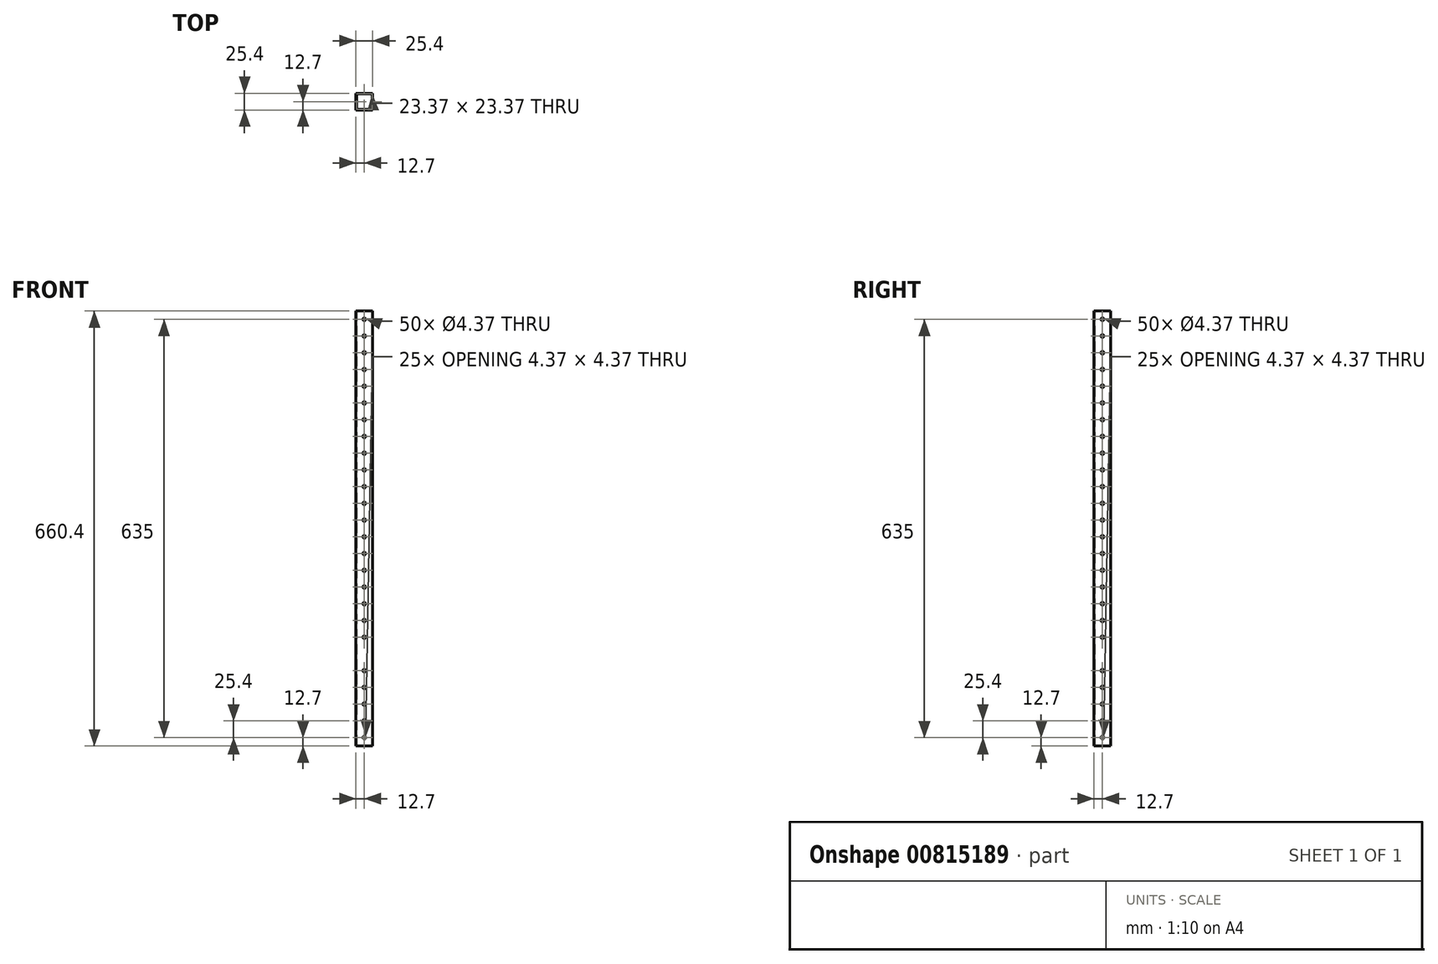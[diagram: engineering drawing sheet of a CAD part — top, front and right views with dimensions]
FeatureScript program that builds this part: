
annotation { "Feature Type Name" : "Feature", "Feature Type Description" : "" }
export const myFeature = defineFeature(function(context is Context, id is Id, definition is map)
    precondition{}
    {
        {
            var Q0;
            Q0=qCreatedBy(makeId("Top.planeOp"),FACE);
            var sketch = newSketch(context, id + "F0", { "sketchPlane" : qUnion([Q0])});
            skLineSegment(sketch, "E0.bottom", {"start": v(0, 0) * mm, "end": v(25.4, 0) * mm});
            skLineSegment(sketch, "E0.top", {"start": v(0, -25.4) * mm, "end": v(25.4, -25.4) * mm});
            skLineSegment(sketch, "E0.left", {"start": v(0, 0) * mm, "end": v(0, -25.4) * mm});
            skLineSegment(sketch, "E0.right", {"start": v(25.4, 0) * mm, "end": v(25.4, -25.4) * mm});
            skLineSegment(sketch, "E1.bottom", {"start": v(1.02, -1.02) * mm, "end": v(24.38, -1.02) * mm});
            skLineSegment(sketch, "E1.top", {"start": v(1.02, -24.38) * mm, "end": v(24.38, -24.38) * mm});
            skLineSegment(sketch, "E1.left", {"start": v(1.02, -1.02) * mm, "end": v(1.02, -24.38) * mm});
            skLineSegment(sketch, "E1.right", {"start": v(24.38, -1.02) * mm, "end": v(24.38, -24.38) * mm});
            skSolve(sketch);
        }
        {
            var Q0;
            Q0=makeQuery(id+"F0.imprint","IMPRINT",FACE,{"disambiguationData":[TD([[makeQuery(id+"F0.imprint","IMPRINT",EDGE,{"derivedFrom":sQuery(id+"F0.wireOp",EDGE,"E0.bottom")}),-1.0]])]});
            extrude(context, id + "F1", {"entities" : qUnion([Q0]), "depth" : 508 * mm, "offsetDistance" : 25.4 * mm});
        }
        {
            var Q0;
            Q0=makeQuery(id+"F1.opExtrude","SWEPT_FACE",FACE,{"disambiguationData":[OSD([sQuery(id+"F0.wireOp",EDGE,"E0.top")])]});
            var sketch = newSketch(context, id + "F2", { "sketchPlane" : qUnion([Q0])});
            skCircle(sketch, "E2", {"center": v(12.7, 12.7) * mm, "radius": 2.18 * mm});
            skCircle(sketch, "E3.0.1.0", {"center": v(12.7, 38.1) * mm, "radius": 2.18 * mm});
            skCircle(sketch, "E3.0.2.0", {"center": v(12.7, 63.5) * mm, "radius": 2.18 * mm});
            skCircle(sketch, "E3.0.3.0", {"center": v(12.7, 88.9) * mm, "radius": 2.18 * mm});
            skCircle(sketch, "E3.0.4.0", {"center": v(12.7, 114.3) * mm, "radius": 2.18 * mm});
            skCircle(sketch, "E3.0.5.0", {"center": v(12.7, 139.7) * mm, "radius": 2.18 * mm});
            skCircle(sketch, "E3.0.6.0", {"center": v(12.7, 165.1) * mm, "radius": 2.18 * mm});
            skCircle(sketch, "E3.0.7.0", {"center": v(12.7, 190.5) * mm, "radius": 2.18 * mm});
            skCircle(sketch, "E3.0.8.0", {"center": v(12.7, 215.9) * mm, "radius": 2.18 * mm});
            skCircle(sketch, "E3.0.9.0", {"center": v(12.7, 241.3) * mm, "radius": 2.18 * mm});
            skCircle(sketch, "E3.0.10.0", {"center": v(12.7, 266.7) * mm, "radius": 2.18 * mm});
            skCircle(sketch, "E3.0.11.0", {"center": v(12.7, 292.1) * mm, "radius": 2.18 * mm});
            skCircle(sketch, "E3.0.12.0", {"center": v(12.7, 317.5) * mm, "radius": 2.18 * mm});
            skCircle(sketch, "E3.0.13.0", {"center": v(12.7, 342.9) * mm, "radius": 2.18 * mm});
            skCircle(sketch, "E3.0.14.0", {"center": v(12.7, 368.3) * mm, "radius": 2.18 * mm});
            skCircle(sketch, "E3.0.15.0", {"center": v(12.7, 393.7) * mm, "radius": 2.18 * mm});
            skCircle(sketch, "E3.0.16.0", {"center": v(12.7, 419.1) * mm, "radius": 2.18 * mm});
            skCircle(sketch, "E3.0.17.0", {"center": v(12.7, 444.5) * mm, "radius": 2.18 * mm});
            skCircle(sketch, "E3.0.18.0", {"center": v(12.7, 469.9) * mm, "radius": 2.18 * mm});
            skCircle(sketch, "E3.0.19.0", {"center": v(12.7, 495.3) * mm, "radius": 2.18 * mm});
            skCircle(sketch, "E3.0.20.0", {"center": v(12.7, 520.7) * mm, "radius": 2.18 * mm});
            skCircle(sketch, "E3.0.21.0", {"center": v(12.7, 546.1) * mm, "radius": 2.18 * mm});
            skCircle(sketch, "E3.0.22.0", {"center": v(12.7, 571.5) * mm, "radius": 2.18 * mm});
            skCircle(sketch, "E3.0.23.0", {"center": v(12.7, 596.9) * mm, "radius": 2.18 * mm});
            skCircle(sketch, "E3.0.24.0", {"center": v(12.7, 622.3) * mm, "radius": 2.18 * mm});
            skLineSegment(sketch, "E3.direction1", {"start": v(12.7, 12.7) * mm, "end": v(38.1, 12.7) * mm, "construction": true});
            skLineSegment(sketch, "E3.direction2", {"start": v(12.7, 12.7) * mm, "end": v(12.7, 38.1) * mm, "construction": true});
            skSolve(sketch);
        }
        {
            var Q0;
            Q0=makeQuery(id+"F2.imprint","IMPRINT",FACE,{"disambiguationData":[TD([[makeQuery(id+"F2.imprint","IMPRINT",EDGE,{"derivedFrom":sQuery(id+"F2.wireOp",EDGE,"E2")}),1.0]])]});
            var Q1;
            Q1=makeQuery(id+"F2.imprint","IMPRINT",FACE,{"disambiguationData":[TD([[makeQuery(id+"F2.imprint","IMPRINT",EDGE,{"derivedFrom":sQuery(id+"F2.wireOp",EDGE,"E3.0.1.0")}),1.0]])]});
            var Q2;
            Q2=makeQuery(id+"F2.imprint","IMPRINT",FACE,{"disambiguationData":[TD([[makeQuery(id+"F2.imprint","IMPRINT",EDGE,{"derivedFrom":sQuery(id+"F2.wireOp",EDGE,"E3.0.9.0")}),1.0]])]});
            var Q3;
            Q3=makeQuery(id+"F2.imprint","IMPRINT",FACE,{"disambiguationData":[TD([[makeQuery(id+"F2.imprint","IMPRINT",EDGE,{"derivedFrom":sQuery(id+"F2.wireOp",EDGE,"E3.0.8.0")}),1.0]])]});
            var Q4;
            Q4=makeQuery(id+"F2.imprint","IMPRINT",FACE,{"disambiguationData":[TD([[makeQuery(id+"F2.imprint","IMPRINT",EDGE,{"derivedFrom":sQuery(id+"F2.wireOp",EDGE,"E3.0.7.0")}),1.0]])]});
            var Q5;
            Q5=makeQuery(id+"F2.imprint","IMPRINT",FACE,{"disambiguationData":[TD([[makeQuery(id+"F2.imprint","IMPRINT",EDGE,{"derivedFrom":sQuery(id+"F2.wireOp",EDGE,"E3.0.6.0")}),1.0]])]});
            var Q6;
            Q6=makeQuery(id+"F2.imprint","IMPRINT",FACE,{"disambiguationData":[TD([[makeQuery(id+"F2.imprint","IMPRINT",EDGE,{"derivedFrom":sQuery(id+"F2.wireOp",EDGE,"E3.0.5.0")}),1.0]])]});
            var Q7;
            Q7=makeQuery(id+"F2.imprint","IMPRINT",FACE,{"disambiguationData":[TD([[makeQuery(id+"F2.imprint","IMPRINT",EDGE,{"derivedFrom":sQuery(id+"F2.wireOp",EDGE,"E3.0.4.0")}),1.0]])]});
            var Q8;
            Q8=makeQuery(id+"F2.imprint","IMPRINT",FACE,{"disambiguationData":[TD([[makeQuery(id+"F2.imprint","IMPRINT",EDGE,{"derivedFrom":sQuery(id+"F2.wireOp",EDGE,"E3.0.3.0")}),1.0]])]});
            var Q9;
            Q9=makeQuery(id+"F2.imprint","IMPRINT",FACE,{"disambiguationData":[TD([[makeQuery(id+"F2.imprint","IMPRINT",EDGE,{"derivedFrom":sQuery(id+"F2.wireOp",EDGE,"E3.0.2.0")}),1.0]])]});
            var Q10;
            Q10=makeQuery(id+"F2.imprint","IMPRINT",FACE,{"disambiguationData":[TD([[makeQuery(id+"F2.imprint","IMPRINT",EDGE,{"derivedFrom":sQuery(id+"F2.wireOp",EDGE,"E3.0.10.0")}),1.0]])]});
            var Q11;
            Q11=makeQuery(id+"F2.imprint","IMPRINT",FACE,{"disambiguationData":[TD([[makeQuery(id+"F2.imprint","IMPRINT",EDGE,{"derivedFrom":sQuery(id+"F2.wireOp",EDGE,"E3.0.11.0")}),1.0]])]});
            var Q12;
            Q12=makeQuery(id+"F2.imprint","IMPRINT",FACE,{"disambiguationData":[TD([[makeQuery(id+"F2.imprint","IMPRINT",EDGE,{"derivedFrom":sQuery(id+"F2.wireOp",EDGE,"E3.0.12.0")}),1.0]])]});
            var Q13;
            Q13=makeQuery(id+"F2.imprint","IMPRINT",FACE,{"disambiguationData":[TD([[makeQuery(id+"F2.imprint","IMPRINT",EDGE,{"derivedFrom":sQuery(id+"F2.wireOp",EDGE,"E3.0.13.0")}),1.0]])]});
            var Q14;
            Q14=makeQuery(id+"F2.imprint","IMPRINT",FACE,{"disambiguationData":[TD([[makeQuery(id+"F2.imprint","IMPRINT",EDGE,{"derivedFrom":sQuery(id+"F2.wireOp",EDGE,"E3.0.14.0")}),1.0]])]});
            var Q15;
            Q15=makeQuery(id+"F2.imprint","IMPRINT",FACE,{"disambiguationData":[TD([[makeQuery(id+"F2.imprint","IMPRINT",EDGE,{"derivedFrom":sQuery(id+"F2.wireOp",EDGE,"E3.0.15.0")}),1.0]])]});
            var Q16;
            Q16=makeQuery(id+"F2.imprint","IMPRINT",FACE,{"disambiguationData":[TD([[makeQuery(id+"F2.imprint","IMPRINT",EDGE,{"derivedFrom":sQuery(id+"F2.wireOp",EDGE,"E3.0.16.0")}),1.0]])]});
            var Q17;
            Q17=makeQuery(id+"F2.imprint","IMPRINT",FACE,{"disambiguationData":[TD([[makeQuery(id+"F2.imprint","IMPRINT",EDGE,{"derivedFrom":sQuery(id+"F2.wireOp",EDGE,"E3.0.17.0")}),1.0]])]});
            var Q18;
            Q18=makeQuery(id+"F2.imprint","IMPRINT",FACE,{"disambiguationData":[TD([[makeQuery(id+"F2.imprint","IMPRINT",EDGE,{"derivedFrom":sQuery(id+"F2.wireOp",EDGE,"E3.0.18.0")}),1.0]])]});
            var Q19;
            Q19=makeQuery(id+"F2.imprint","IMPRINT",FACE,{"disambiguationData":[TD([[makeQuery(id+"F2.imprint","IMPRINT",EDGE,{"derivedFrom":sQuery(id+"F2.wireOp",EDGE,"E3.0.19.0")}),1.0]])]});
            var Q20;
            Q20=makeQuery(id+"F2.imprint","IMPRINT",FACE,{"disambiguationData":[TD([[makeQuery(id+"F2.imprint","IMPRINT",EDGE,{"derivedFrom":sQuery(id+"F2.wireOp",EDGE,"E3.0.20.0")}),1.0]])]});
            var Q21;
            Q21=makeQuery(id+"F2.imprint","IMPRINT",FACE,{"disambiguationData":[TD([[makeQuery(id+"F2.imprint","IMPRINT",EDGE,{"derivedFrom":sQuery(id+"F2.wireOp",EDGE,"E3.0.21.0")}),1.0]])]});
            var Q22;
            Q22=makeQuery(id+"F2.imprint","IMPRINT",FACE,{"disambiguationData":[TD([[makeQuery(id+"F2.imprint","IMPRINT",EDGE,{"derivedFrom":sQuery(id+"F2.wireOp",EDGE,"E3.0.22.0")}),1.0]])]});
            var Q23;
            Q23=makeQuery(id+"F2.imprint","IMPRINT",FACE,{"disambiguationData":[TD([[makeQuery(id+"F2.imprint","IMPRINT",EDGE,{"derivedFrom":sQuery(id+"F2.wireOp",EDGE,"E3.0.23.0")}),1.0]])]});
            var Q24;
            Q24=makeQuery(id+"F2.imprint","IMPRINT",FACE,{"disambiguationData":[TD([[makeQuery(id+"F2.imprint","IMPRINT",EDGE,{"derivedFrom":sQuery(id+"F2.wireOp",EDGE,"E3.0.24.0")}),1.0]])]});
            extrude(context, id + "F3", {"entities" : qUnion([Q0, Q1, Q2, Q3, Q4, Q5, Q6, Q7, Q8, Q9, Q10, Q11, Q12, Q13, Q14, Q15, Q16, Q17, Q18, Q19, Q20, Q21, Q22, Q23, Q24]), "operationType" : NewBodyOperationType.REMOVE, "oppositeDirection" : true, "depth" : 25.4 * mm, "offsetDistance" : 25.4 * mm});
        }
        {
            var Q0;
            Q0=makeQuery(id+"F1.opExtrude","SWEPT_FACE",FACE,{"disambiguationData":[OSD([sQuery(id+"F0.wireOp",EDGE,"E0.left")])]});
            var sketch = newSketch(context, id + "F4", { "sketchPlane" : qUnion([Q0])});
            skCircle(sketch, "E4", {"center": v(12.7, 12.7) * mm, "radius": 2.18 * mm});
            skCircle(sketch, "E5.0.1.0", {"center": v(12.7, 38.1) * mm, "radius": 2.18 * mm});
            skCircle(sketch, "E5.0.2.0", {"center": v(12.7, 63.5) * mm, "radius": 2.18 * mm});
            skCircle(sketch, "E5.0.3.0", {"center": v(12.7, 88.9) * mm, "radius": 2.18 * mm});
            skCircle(sketch, "E5.0.4.0", {"center": v(12.7, 114.3) * mm, "radius": 2.18 * mm});
            skCircle(sketch, "E5.0.5.0", {"center": v(12.7, 139.7) * mm, "radius": 2.18 * mm});
            skCircle(sketch, "E5.0.6.0", {"center": v(12.7, 165.1) * mm, "radius": 2.18 * mm});
            skCircle(sketch, "E5.0.7.0", {"center": v(12.7, 190.5) * mm, "radius": 2.18 * mm});
            skCircle(sketch, "E5.0.8.0", {"center": v(12.7, 215.9) * mm, "radius": 2.18 * mm});
            skCircle(sketch, "E5.0.9.0", {"center": v(12.7, 241.3) * mm, "radius": 2.18 * mm});
            skCircle(sketch, "E5.0.10.0", {"center": v(12.7, 266.7) * mm, "radius": 2.18 * mm});
            skCircle(sketch, "E5.0.11.0", {"center": v(12.7, 292.1) * mm, "radius": 2.18 * mm});
            skCircle(sketch, "E5.0.12.0", {"center": v(12.7, 317.5) * mm, "radius": 2.18 * mm});
            skCircle(sketch, "E5.0.13.0", {"center": v(12.7, 342.9) * mm, "radius": 2.18 * mm});
            skCircle(sketch, "E5.0.14.0", {"center": v(12.7, 368.3) * mm, "radius": 2.18 * mm});
            skCircle(sketch, "E5.0.15.0", {"center": v(12.7, 393.7) * mm, "radius": 2.18 * mm});
            skCircle(sketch, "E5.0.16.0", {"center": v(12.7, 419.1) * mm, "radius": 2.18 * mm});
            skCircle(sketch, "E5.0.17.0", {"center": v(12.7, 444.5) * mm, "radius": 2.18 * mm});
            skCircle(sketch, "E5.0.18.0", {"center": v(12.7, 469.9) * mm, "radius": 2.18 * mm});
            skCircle(sketch, "E5.0.19.0", {"center": v(12.7, 495.3) * mm, "radius": 2.18 * mm});
            skCircle(sketch, "E5.0.20.0", {"center": v(12.7, 520.7) * mm, "radius": 2.18 * mm});
            skCircle(sketch, "E5.0.21.0", {"center": v(12.7, 546.1) * mm, "radius": 2.18 * mm});
            skCircle(sketch, "E5.0.22.0", {"center": v(12.7, 571.5) * mm, "radius": 2.18 * mm});
            skCircle(sketch, "E5.0.23.0", {"center": v(12.7, 596.9) * mm, "radius": 2.18 * mm});
            skCircle(sketch, "E5.0.24.0", {"center": v(12.7, 622.3) * mm, "radius": 2.18 * mm});
            skLineSegment(sketch, "E5.direction1", {"start": v(12.7, 12.7) * mm, "end": v(38.1, 12.7) * mm, "construction": true});
            skLineSegment(sketch, "E5.direction2", {"start": v(12.7, 12.7) * mm, "end": v(12.7, 38.1) * mm, "construction": true});
            skSolve(sketch);
        }
        {
            var Q0;
            Q0=makeQuery(id+"F4.imprint","IMPRINT",FACE,{"disambiguationData":[TD([[makeQuery(id+"F4.imprint","IMPRINT",EDGE,{"derivedFrom":sQuery(id+"F4.wireOp",EDGE,"E4")}),1.0]])]});
            var Q1;
            Q1=makeQuery(id+"F4.imprint","IMPRINT",FACE,{"disambiguationData":[TD([[makeQuery(id+"F4.imprint","IMPRINT",EDGE,{"derivedFrom":sQuery(id+"F4.wireOp",EDGE,"E5.0.1.0")}),1.0]])]});
            var Q2;
            Q2=makeQuery(id+"F4.imprint","IMPRINT",FACE,{"disambiguationData":[TD([[makeQuery(id+"F4.imprint","IMPRINT",EDGE,{"derivedFrom":sQuery(id+"F4.wireOp",EDGE,"E5.0.2.0")}),1.0]])]});
            var Q3;
            Q3=makeQuery(id+"F4.imprint","IMPRINT",FACE,{"disambiguationData":[TD([[makeQuery(id+"F4.imprint","IMPRINT",EDGE,{"derivedFrom":sQuery(id+"F4.wireOp",EDGE,"E5.0.3.0")}),1.0]])]});
            var Q4;
            Q4=makeQuery(id+"F4.imprint","IMPRINT",FACE,{"disambiguationData":[TD([[makeQuery(id+"F4.imprint","IMPRINT",EDGE,{"derivedFrom":sQuery(id+"F4.wireOp",EDGE,"E5.0.4.0")}),1.0]])]});
            var Q5;
            Q5=makeQuery(id+"F4.imprint","IMPRINT",FACE,{"disambiguationData":[TD([[makeQuery(id+"F4.imprint","IMPRINT",EDGE,{"derivedFrom":sQuery(id+"F4.wireOp",EDGE,"E5.0.5.0")}),1.0]])]});
            var Q6;
            Q6=makeQuery(id+"F4.imprint","IMPRINT",FACE,{"disambiguationData":[TD([[makeQuery(id+"F4.imprint","IMPRINT",EDGE,{"derivedFrom":sQuery(id+"F4.wireOp",EDGE,"E5.0.6.0")}),1.0]])]});
            var Q7;
            Q7=makeQuery(id+"F4.imprint","IMPRINT",FACE,{"disambiguationData":[TD([[makeQuery(id+"F4.imprint","IMPRINT",EDGE,{"derivedFrom":sQuery(id+"F4.wireOp",EDGE,"E5.0.7.0")}),1.0]])]});
            var Q8;
            Q8=makeQuery(id+"F4.imprint","IMPRINT",FACE,{"disambiguationData":[TD([[makeQuery(id+"F4.imprint","IMPRINT",EDGE,{"derivedFrom":sQuery(id+"F4.wireOp",EDGE,"E5.0.8.0")}),1.0]])]});
            var Q9;
            Q9=makeQuery(id+"F4.imprint","IMPRINT",FACE,{"disambiguationData":[TD([[makeQuery(id+"F4.imprint","IMPRINT",EDGE,{"derivedFrom":sQuery(id+"F4.wireOp",EDGE,"E5.0.9.0")}),1.0]])]});
            var Q10;
            Q10=makeQuery(id+"F4.imprint","IMPRINT",FACE,{"disambiguationData":[TD([[makeQuery(id+"F4.imprint","IMPRINT",EDGE,{"derivedFrom":sQuery(id+"F4.wireOp",EDGE,"E5.0.10.0")}),1.0]])]});
            var Q11;
            Q11=makeQuery(id+"F4.imprint","IMPRINT",FACE,{"disambiguationData":[TD([[makeQuery(id+"F4.imprint","IMPRINT",EDGE,{"derivedFrom":sQuery(id+"F4.wireOp",EDGE,"E5.0.11.0")}),1.0]])]});
            var Q12;
            Q12=makeQuery(id+"F4.imprint","IMPRINT",FACE,{"disambiguationData":[TD([[makeQuery(id+"F4.imprint","IMPRINT",EDGE,{"derivedFrom":sQuery(id+"F4.wireOp",EDGE,"E5.0.12.0")}),1.0]])]});
            var Q13;
            Q13=makeQuery(id+"F4.imprint","IMPRINT",FACE,{"disambiguationData":[TD([[makeQuery(id+"F4.imprint","IMPRINT",EDGE,{"derivedFrom":sQuery(id+"F4.wireOp",EDGE,"E5.0.13.0")}),1.0]])]});
            var Q14;
            Q14=makeQuery(id+"F4.imprint","IMPRINT",FACE,{"disambiguationData":[TD([[makeQuery(id+"F4.imprint","IMPRINT",EDGE,{"derivedFrom":sQuery(id+"F4.wireOp",EDGE,"E5.0.14.0")}),1.0]])]});
            var Q15;
            Q15=makeQuery(id+"F4.imprint","IMPRINT",FACE,{"disambiguationData":[TD([[makeQuery(id+"F4.imprint","IMPRINT",EDGE,{"derivedFrom":sQuery(id+"F4.wireOp",EDGE,"E5.0.15.0")}),1.0]])]});
            var Q16;
            Q16=makeQuery(id+"F4.imprint","IMPRINT",FACE,{"disambiguationData":[TD([[makeQuery(id+"F4.imprint","IMPRINT",EDGE,{"derivedFrom":sQuery(id+"F4.wireOp",EDGE,"E5.0.16.0")}),1.0]])]});
            var Q17;
            Q17=makeQuery(id+"F4.imprint","IMPRINT",FACE,{"disambiguationData":[TD([[makeQuery(id+"F4.imprint","IMPRINT",EDGE,{"derivedFrom":sQuery(id+"F4.wireOp",EDGE,"E5.0.17.0")}),1.0]])]});
            var Q18;
            Q18=makeQuery(id+"F4.imprint","IMPRINT",FACE,{"disambiguationData":[TD([[makeQuery(id+"F4.imprint","IMPRINT",EDGE,{"derivedFrom":sQuery(id+"F4.wireOp",EDGE,"E5.0.21.0")}),1.0]])]});
            var Q19;
            Q19=makeQuery(id+"F4.imprint","IMPRINT",FACE,{"disambiguationData":[TD([[makeQuery(id+"F4.imprint","IMPRINT",EDGE,{"derivedFrom":sQuery(id+"F4.wireOp",EDGE,"E5.0.20.0")}),1.0]])]});
            var Q20;
            Q20=makeQuery(id+"F4.imprint","IMPRINT",FACE,{"disambiguationData":[TD([[makeQuery(id+"F4.imprint","IMPRINT",EDGE,{"derivedFrom":sQuery(id+"F4.wireOp",EDGE,"E5.0.19.0")}),1.0]])]});
            var Q21;
            Q21=makeQuery(id+"F4.imprint","IMPRINT",FACE,{"disambiguationData":[TD([[makeQuery(id+"F4.imprint","IMPRINT",EDGE,{"derivedFrom":sQuery(id+"F4.wireOp",EDGE,"E5.0.18.0")}),1.0]])]});
            var Q22;
            Q22=makeQuery(id+"F4.imprint","IMPRINT",FACE,{"disambiguationData":[TD([[makeQuery(id+"F4.imprint","IMPRINT",EDGE,{"derivedFrom":sQuery(id+"F4.wireOp",EDGE,"E5.0.22.0")}),1.0]])]});
            var Q23;
            Q23=makeQuery(id+"F4.imprint","IMPRINT",FACE,{"disambiguationData":[TD([[makeQuery(id+"F4.imprint","IMPRINT",EDGE,{"derivedFrom":sQuery(id+"F4.wireOp",EDGE,"E5.0.23.0")}),1.0]])]});
            var Q24;
            Q24=makeQuery(id+"F4.imprint","IMPRINT",FACE,{"disambiguationData":[TD([[makeQuery(id+"F4.imprint","IMPRINT",EDGE,{"derivedFrom":sQuery(id+"F4.wireOp",EDGE,"E5.0.24.0")}),1.0]])]});
            extrude(context, id + "F5", {"entities" : qUnion([Q0, Q1, Q2, Q3, Q4, Q5, Q6, Q7, Q8, Q9, Q10, Q11, Q12, Q13, Q14, Q15, Q16, Q17, Q18, Q19, Q20, Q21, Q22, Q23, Q24]), "operationType" : NewBodyOperationType.REMOVE, "oppositeDirection" : true, "depth" : 25.4 * mm, "offsetDistance" : 25.4 * mm});
        }
        {
            var Q0;
            Q0=makeQuery(id+"F1.opExtrude","CAP_FACE",FACE,{"disambiguationData":[OSD([sQuery(id+"F0.wireOp",EDGE,"E0.bottom"),sQuery(id+"F0.wireOp",EDGE,"E0.top"),sQuery(id+"F0.wireOp",EDGE,"E0.left"),sQuery(id+"F0.wireOp",EDGE,"E0.right"),sQuery(id+"F0.wireOp",EDGE,"E1.bottom"),sQuery(id+"F0.wireOp",EDGE,"E1.top"),sQuery(id+"F0.wireOp",EDGE,"E1.left"),sQuery(id+"F0.wireOp",EDGE,"E1.right")])],"isStart":true});
            extrude(context, id + "F6", {"entities" : qUnion([Q0]), "operationType" : NewBodyOperationType.ADD, "depth" : 152.4 * mm, "offsetDistance" : 25.4 * mm});
        }
        {
            var Q0;
            {var subQ0=sQuery(id+"F0.wireOp",EDGE,"E0.top");Q0=makeQuery(id+"F6.boolean.opBoolean","MERGE",FACE,{"derivedFrom":[makeQuery(id+"F1.opExtrude","SWEPT_FACE",FACE,{"disambiguationData":[OSD([subQ0])]}),makeQuery(id+"F6.opExtrude","SWEPT_FACE",FACE,{"disambiguationData":[OSD([subQ0])]})]});}
            var sketch = newSketch(context, id + "F7", { "sketchPlane" : qUnion([Q0])});
            skCircle(sketch, "E6", {"center": v(12.7, -139.7) * mm, "radius": 2.18 * mm});
            skCircle(sketch, "E7.0.1.0", {"center": v(12.7, -114.3) * mm, "radius": 2.18 * mm});
            skCircle(sketch, "E7.0.2.0", {"center": v(12.7, -88.9) * mm, "radius": 2.18 * mm});
            skCircle(sketch, "E7.0.3.0", {"center": v(12.7, -63.5) * mm, "radius": 2.18 * mm});
            skCircle(sketch, "E7.0.4.0", {"center": v(12.7, -38.1) * mm, "radius": 2.18 * mm});
            skLineSegment(sketch, "E7.direction1", {"start": v(12.7, -139.7) * mm, "end": v(38.1, -139.7) * mm, "construction": true});
            skLineSegment(sketch, "E7.direction2", {"start": v(12.7, -139.7) * mm, "end": v(12.7, -114.3) * mm, "construction": true});
            skSolve(sketch);
        }
        {
            var Q0;
            Q0=makeQuery(id+"F7.imprint","IMPRINT",FACE,{"disambiguationData":[TD([[makeQuery(id+"F7.imprint","IMPRINT",EDGE,{"derivedFrom":sQuery(id+"F7.wireOp",EDGE,"E7.0.4.0")}),1.0]])]});
            var Q1;
            Q1=makeQuery(id+"F7.imprint","IMPRINT",FACE,{"disambiguationData":[TD([[makeQuery(id+"F7.imprint","IMPRINT",EDGE,{"derivedFrom":sQuery(id+"F7.wireOp",EDGE,"E7.0.3.0")}),1.0]])]});
            var Q2;
            Q2=makeQuery(id+"F7.imprint","IMPRINT",FACE,{"disambiguationData":[TD([[makeQuery(id+"F7.imprint","IMPRINT",EDGE,{"derivedFrom":sQuery(id+"F7.wireOp",EDGE,"E7.0.2.0")}),1.0]])]});
            var Q3;
            Q3=makeQuery(id+"F7.imprint","IMPRINT",FACE,{"disambiguationData":[TD([[makeQuery(id+"F7.imprint","IMPRINT",EDGE,{"derivedFrom":sQuery(id+"F7.wireOp",EDGE,"E7.0.1.0")}),1.0]])]});
            var Q4;
            Q4=makeQuery(id+"F7.imprint","IMPRINT",FACE,{"disambiguationData":[TD([[makeQuery(id+"F7.imprint","IMPRINT",EDGE,{"derivedFrom":sQuery(id+"F7.wireOp",EDGE,"E6")}),1.0]])]});
            extrude(context, id + "F8", {"entities" : qUnion([Q0, Q1, Q2, Q3, Q4]), "operationType" : NewBodyOperationType.REMOVE, "oppositeDirection" : true, "depth" : 25.4 * mm, "offsetDistance" : 25.4 * mm});
        }
        {
            var Q0;
            {var subQ0=sQuery(id+"F0.wireOp",EDGE,"E0.left");Q0=makeQuery(id+"F6.boolean.opBoolean","MERGE",FACE,{"derivedFrom":[makeQuery(id+"F1.opExtrude","SWEPT_FACE",FACE,{"disambiguationData":[OSD([subQ0])]}),makeQuery(id+"F6.opExtrude","SWEPT_FACE",FACE,{"disambiguationData":[OSD([subQ0])]})]});}
            var sketch = newSketch(context, id + "F9", { "sketchPlane" : qUnion([Q0])});
            skCircle(sketch, "E8", {"center": v(12.7, -139.7) * mm, "radius": 2.18 * mm});
            skCircle(sketch, "E9.0.1.0", {"center": v(12.7, -114.3) * mm, "radius": 2.18 * mm});
            skCircle(sketch, "E9.0.2.0", {"center": v(12.7, -88.9) * mm, "radius": 2.18 * mm});
            skCircle(sketch, "E9.0.3.0", {"center": v(12.7, -63.5) * mm, "radius": 2.18 * mm});
            skCircle(sketch, "E9.0.4.0", {"center": v(12.7, -38.1) * mm, "radius": 2.18 * mm});
            skLineSegment(sketch, "E9.direction1", {"start": v(12.7, -139.7) * mm, "end": v(38.1, -139.7) * mm, "construction": true});
            skLineSegment(sketch, "E9.direction2", {"start": v(12.7, -139.7) * mm, "end": v(12.7, -114.3) * mm, "construction": true});
            skSolve(sketch);
        }
        {
            var Q0;
            Q0=makeQuery(id+"F9.imprint","IMPRINT",FACE,{"disambiguationData":[TD([[makeQuery(id+"F9.imprint","IMPRINT",EDGE,{"derivedFrom":sQuery(id+"F9.wireOp",EDGE,"E9.0.4.0")}),1.0]])]});
            var Q1;
            Q1=makeQuery(id+"F9.imprint","IMPRINT",FACE,{"disambiguationData":[TD([[makeQuery(id+"F9.imprint","IMPRINT",EDGE,{"derivedFrom":sQuery(id+"F9.wireOp",EDGE,"E9.0.3.0")}),1.0]])]});
            var Q2;
            Q2=makeQuery(id+"F9.imprint","IMPRINT",FACE,{"disambiguationData":[TD([[makeQuery(id+"F9.imprint","IMPRINT",EDGE,{"derivedFrom":sQuery(id+"F9.wireOp",EDGE,"E9.0.2.0")}),1.0]])]});
            var Q3;
            Q3=makeQuery(id+"F9.imprint","IMPRINT",FACE,{"disambiguationData":[TD([[makeQuery(id+"F9.imprint","IMPRINT",EDGE,{"derivedFrom":sQuery(id+"F9.wireOp",EDGE,"E9.0.1.0")}),1.0]])]});
            var Q4;
            Q4=makeQuery(id+"F9.imprint","IMPRINT",FACE,{"disambiguationData":[TD([[makeQuery(id+"F9.imprint","IMPRINT",EDGE,{"derivedFrom":sQuery(id+"F9.wireOp",EDGE,"E8")}),1.0]])]});
            extrude(context, id + "F10", {"entities" : qUnion([Q0, Q1, Q2, Q3, Q4]), "operationType" : NewBodyOperationType.REMOVE, "oppositeDirection" : true, "depth" : 25.4 * mm, "offsetDistance" : 25.4 * mm});
        }
    });
